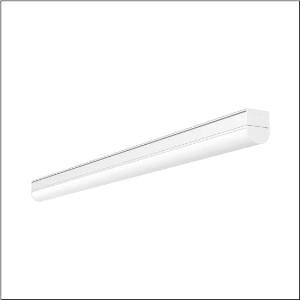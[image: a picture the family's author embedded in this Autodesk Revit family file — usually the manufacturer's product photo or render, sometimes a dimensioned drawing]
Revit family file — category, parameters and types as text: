
# Revit family: ecopack_r__31_51lj12mnm70a_41d1
name_source: partatom
category: Lighting Fixtures
units: mm (PartAtom-declared; Revit-internal decimal feet)

## family parameters
Cut with Voids When Loaded = No
Host = Face
Light Source = No
Part Type = Normal
Room Calculation Point = No
Round Connector Dimension = Use Diameter
Shared = No

## types (1)
- --- (1 x LED, 6780 lm, 50 W, 5000K)
    Apparent Load = 50 VA
    CIE Flux Codes = 39 67 87 89 100
    Color Rendering = 80
    Color Temperature = 5000K
    Default Elevation = 1800 mm
    Description = Ecopack® 31, diffuser luminaire, primary optical cover: cover, of PC, frosted, light emission: direct distribution, primary light characteristic: symmetric, installation type: surface-mounted, LED, rated luminous flux: 7.000lm, luminous efficacy: 140lm/W, light colour: 830/840/850, colour temperature: 3000/4000/5000K, control gear: ECG, with terminal, 3-pole, mains connection: 220..240V, AC, 50/60Hz, rated input power: 50W, housing, of aluminium, traffic white (RAL 9016), length: 1.450mm, width: 56mm, height: 68mm, end cap, of PC, white, protection rating (complete): IP20, insulation class (complete): insulation class I (protective earthing), certification: CE, impact resistance: IK06, permissible operating ambient temperature: -20..+40°C, packaging unit: 1 piece
    Height = 68 mm
    Lamp = 1 x LED
    Lamp Light Flux = 6780 lm
    Lamp Power = 50 W
    Lamp count = 1
    Length = 1450 mm
    Luminous efficacy = 136 lm/W
    Manufacturer = Siteco
    ModVariant = No
    Model = 51LJ12MNM70A
    Mounting Place = Ceiling
    Mounting Type = Surface mounted
    Number of Poles = 1
    OnlyDefault = Yes
    Power Factor = 1
    Product Name = Ecopack® 31
    Product group = diffuser luminaire
    ProductGroupID = 303
    Protection Class = Protection class I
    Protection Degree = IP 20
    RLX_Detail_Level = 1
    RLX_Emergency_Light_Flux = 0 lm
    RLX_Emergency_Type = 0
    RLX_Emergency_Type_DB = No
    RlxData = <blob elided: 39329 chars, md5=92efcd1f>
    Socket = socket
    Standby Power = 0 W
    System Light Flux = 6780 lm
    System Power = 50 W
    Type Comments = individual setting: colour temperature 5000K, luminous flux: 100 % | (ON | ON)
    Type Image = l_1007033.jpg
    URL = http://relux.com
    VarID = @adj_107049
    Voltage = 0 V
    Weight = 0.00 kg
    Width = 56 mm  [stored 0.183727 ft]

note: [stored X ft] marks values corroborated as IEEE doubles in the binary element streams (Revit-internal decimal feet)

## geometry (parser evidence)
native form markers: Blend x4, Sweep x11
no freeform markers — native parametric forms only
